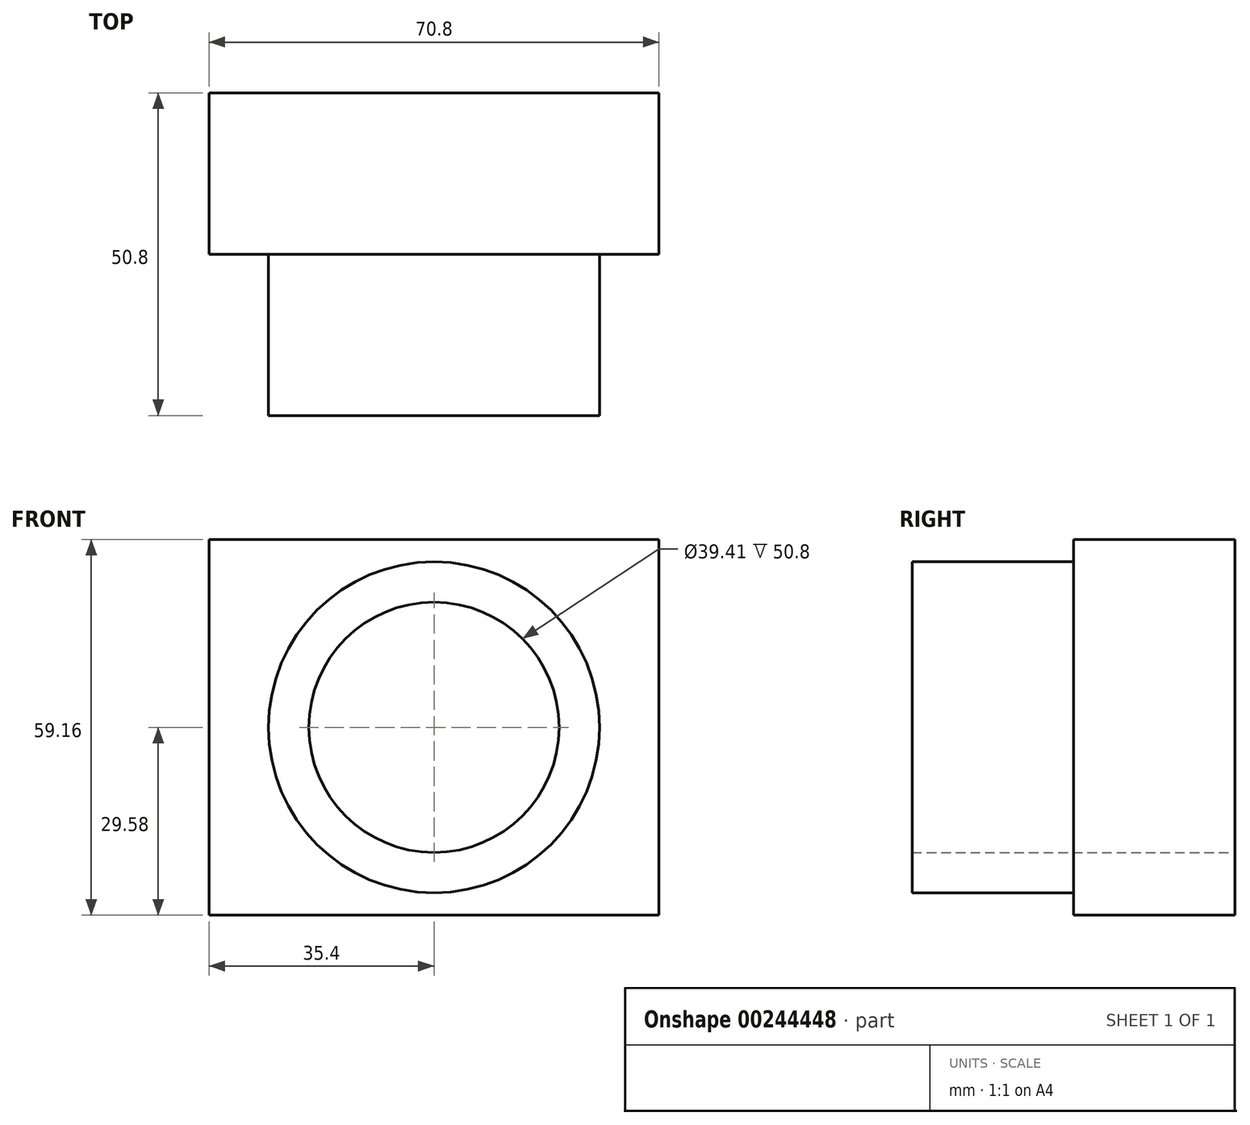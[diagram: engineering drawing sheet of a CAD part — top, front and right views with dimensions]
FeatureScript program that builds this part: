
annotation { "Feature Type Name" : "Feature", "Feature Type Description" : "" }
export const myFeature = defineFeature(function(context is Context, id is Id, definition is map)
    precondition{}
    {
        {
            var Q0;
            Q0=qCreatedBy(makeId("Front.planeOp"),FACE);
            var sketch = newSketch(context, id + "F0", { "sketchPlane" : qUnion([Q0])});
            skLineSegment(sketch, "E0.bottom", {"start": v(35.4, 29.58) * mm, "end": v(-35.4, 29.58) * mm});
            skLineSegment(sketch, "E0.top", {"start": v(35.4, -29.58) * mm, "end": v(-35.4, -29.58) * mm});
            skLineSegment(sketch, "E0.left", {"start": v(35.4, 29.58) * mm, "end": v(35.4, -29.58) * mm});
            skLineSegment(sketch, "E0.right", {"start": v(-35.4, 29.58) * mm, "end": v(-35.4, -29.58) * mm});
            skPoint(sketch, "E0.middle", {"position": v(0, 0) * mm});
            skCircle(sketch, "E1", {"center": v(0, 0) * mm, "radius": 19.7 * mm});
            skSolve(sketch);
        }
        {
            var Q0;
            Q0=makeQuery(id+"F0.imprint","IMPRINT",FACE,{"disambiguationData":[TD([[makeQuery(id+"F0.imprint","IMPRINT",EDGE,{"derivedFrom":sQuery(id+"F0.wireOp",EDGE,"E0.bottom")}),1.0]])]});
            extrude(context, id + "F1", {"entities" : qUnion([Q0]), "depth" : 25.4 * mm});
        }
        {
            var Q0;
            Q0=makeQuery(id+"F1.opExtrude","CAP_FACE",FACE,{"disambiguationData":[OSD([sQuery(id+"F0.wireOp",EDGE,"E0.bottom"),sQuery(id+"F0.wireOp",EDGE,"E0.top"),sQuery(id+"F0.wireOp",EDGE,"E0.left"),sQuery(id+"F0.wireOp",EDGE,"E0.right"),sQuery(id+"F0.wireOp",EDGE,"E1")])],"isStart":false});
            var sketch = newSketch(context, id + "F2", { "sketchPlane" : qUnion([Q0])});
            skCircle(sketch, "E2.0", {"center": v(0, 0) * mm, "radius": 19.7 * mm});
            skCircle(sketch, "E3.0", {"center": v(0, 0) * mm, "radius": 26.05 * mm});
            skSolve(sketch);
        }
        {
            var Q0;
            Q0 = qSketchRegion(id + "F2", true);
            extrude(context, id + "F3", {"entities" : qUnion([Q0]), "operationType" : NewBodyOperationType.ADD, "depth" : 25.4 * mm});
        }
    });
